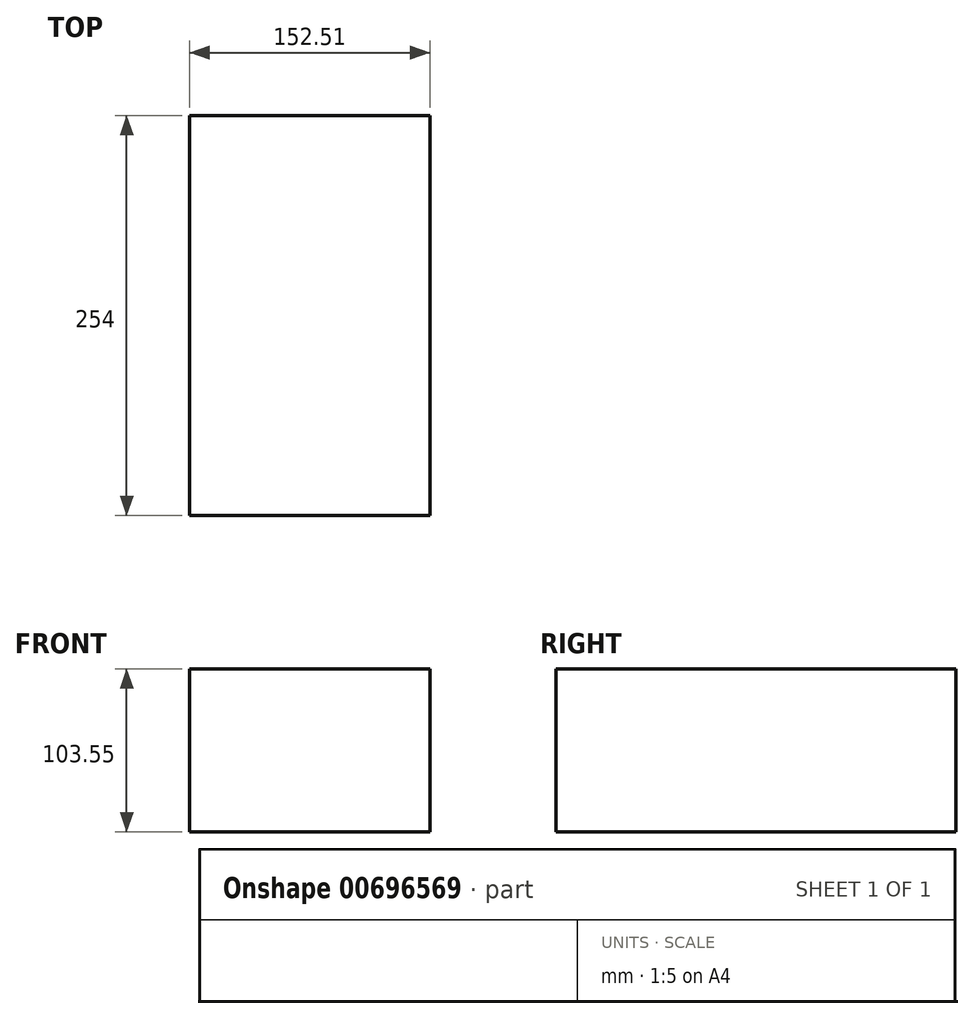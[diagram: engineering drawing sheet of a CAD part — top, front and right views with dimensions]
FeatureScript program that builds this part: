
annotation { "Feature Type Name" : "Feature", "Feature Type Description" : "" }
export const myFeature = defineFeature(function(context is Context, id is Id, definition is map)
    precondition{}
    {
        {
            var Q0;
            Q0=qCreatedBy(makeId("Front.planeOp"),FACE);
            var sketch = newSketch(context, id + "F0", { "sketchPlane" : qUnion([Q0])});
            skLineSegment(sketch, "E0.bottom", {"start": v(0, 0) * mm, "end": v(152.5, 0) * mm});
            skLineSegment(sketch, "E0.top", {"start": v(0, 103.55) * mm, "end": v(152.5, 103.55) * mm});
            skLineSegment(sketch, "E0.left", {"start": v(0, 0) * mm, "end": v(0, 103.55) * mm});
            skLineSegment(sketch, "E0.right", {"start": v(152.5, 0) * mm, "end": v(152.5, 103.55) * mm});
            skSolve(sketch);
        }
        {
            var Q0;
            Q0 = qSketchRegion(id + "F0", true);
            extrude(context, id + "F1", {"entities" : qUnion([Q0]), "depth" : 254 * mm, "offsetDistance" : 25.4 * mm});
        }
    });
